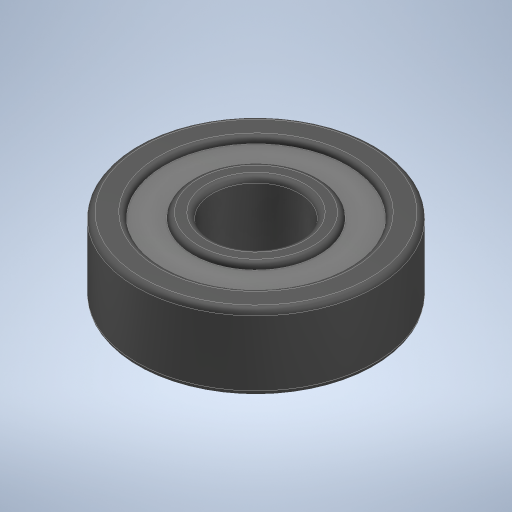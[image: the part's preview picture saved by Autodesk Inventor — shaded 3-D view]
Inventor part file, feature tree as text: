
AUTODESK INVENTOR PART (.ipt)
format: ipt  version: 2023 (Build 270158000, 158)  size: 644,608 bytes
history: native  units: in
note: dims shown in document units (in); Inventor stores cm internally (conversion verified against a paired STEP export)
features: other x7, fillet x2, revolve x1, mirror x1
ambient origin geometry x8: Origin, YZ Plane, XZ Plane, XY Plane, X Axis, Y Axis, Z Axis, Center Point
bodies: Solid1 (feature_tree), Solid2 (feature_tree), Solid3 (feature_tree), Solid4 (feature_tree), Solid5 (feature_tree), Solid6 (feature_tree), Solid7 (feature_tree), Solid8 (feature_tree), Solid9 (feature_tree), Solid10 (feature_tree), Solid11 (feature_tree)
feature tree (11):
  fillet  "Fillet1"  [1 undecoded]
  fillet  "Fillet2"  [1 undecoded]
  revolve  "Revolve1"  [1 undecoded]
  other  "CirPattern2[1]"
  other  "CirPattern2[2]"
  other  "CirPattern2[3]"
  other  "CirPattern2[4]"
  other  "CirPattern2[5]"
  other  "CirPattern2[6]"
  other  "Boss-Extrude4"
  mirror  "Mirror1"
note: 3 required parameter values undecoded (feature->parameter linkage not recoverable at this tier; creation-order binding heuristic only, values carry confidence <= 0.55)
